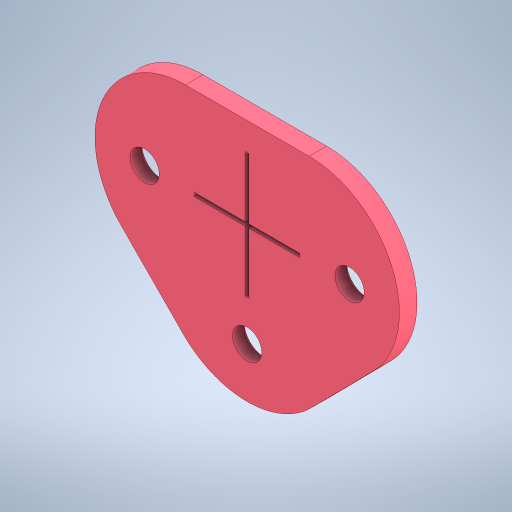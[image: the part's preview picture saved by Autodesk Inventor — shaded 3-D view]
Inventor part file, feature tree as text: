
AUTODESK INVENTOR PART (.ipt)
format: ipt  version: 2023.1 (Build 271208000, 208)  size: 391,168 bytes
history: native  units: mm
features: extrude x6, sketch x6, projected_geometry x3, mirror x2, chamfer x1, boolean_combine x1, pattern_linear x1, fillet x1
ambient origin geometry x8: Origin, YZ Plane, XZ Plane, XY Plane, X Axis, Y Axis, Z Axis, Center Point
bodies: Solid3 (feature_tree)
feature tree (21):
  extrude  "Extrusion3"  Depth=5.0mm
  extrude  "Extrusion4"  Depth=17.162mm
  chamfer  "Chamfer1"  Distance=1.5mm
  extrude  "Extrusion5"  Depth=21.669147mm
  boolean_combine  "Combine1"
  mirror  "Mirror1"
  mirror  "Mirror2"
  extrude  "Extrusion8"  Depth=21.669147mm
  pattern_linear  "Rectangular Pattern1"  Spacing1=4.0mm  [1 undecoded]
  extrude  "Extrusion6"  Depth=21.669147mm
  fillet  "Fillet1"  Radius=4.0mm
  extrude  "Extrusion7"  Depth=2.0mm TaperAngle=0.0deg
  sketch  "Sketch1"  dims[d0=13.0mm d7=5.0mm]
  sketch  "Sketch4"  dims[d8=5.321mm d9=17.162mm]
  projected_geometry  "Projected Loop1"
  sketch  "Sketch5"  dims[d10=5.321mm]
  sketch  "Sketch6"  dims[d11=5.0mm]
  projected_geometry  "Projected Loop2"
  sketch  "Sketch7"  dims[d12=2.218mm]
  sketch  "Sketch8"  dims[d13=12.0mm d14=1.5mm d15=3.3mm d16=4.0mm d17=4.0mm d18=3.3mm d19=4.0mm d20=2.0mm d21=0.0mm d22=0.4mm d23=0.4mm d24=1.5mm d25=0.0mm d26=0.7mm d27=2.0mm d28=45.0deg d32=1.2mm d33=2.0mm d34=0.0mm d35=0.0mm d36=24.0mm d37=39.0mm d38=20.0mm d40=24.0mm d41=0.25mm d42=1.2mm d43=0.0mm d44=2.0mm d45=0.5mm d46=0.0mm d47=0.4mm d48=0.0mm d49=0.0mm d50=3.3mm d51=30.0mm d52=4.6mm d53=1.5mm d54=21.669147mm d55=5.676247mm]
  projected_geometry  "Projected Loop3"
note: 1 required parameter value undecoded (feature->parameter linkage not recoverable at this tier; creation-order binding heuristic only, values carry confidence <= 0.55)
